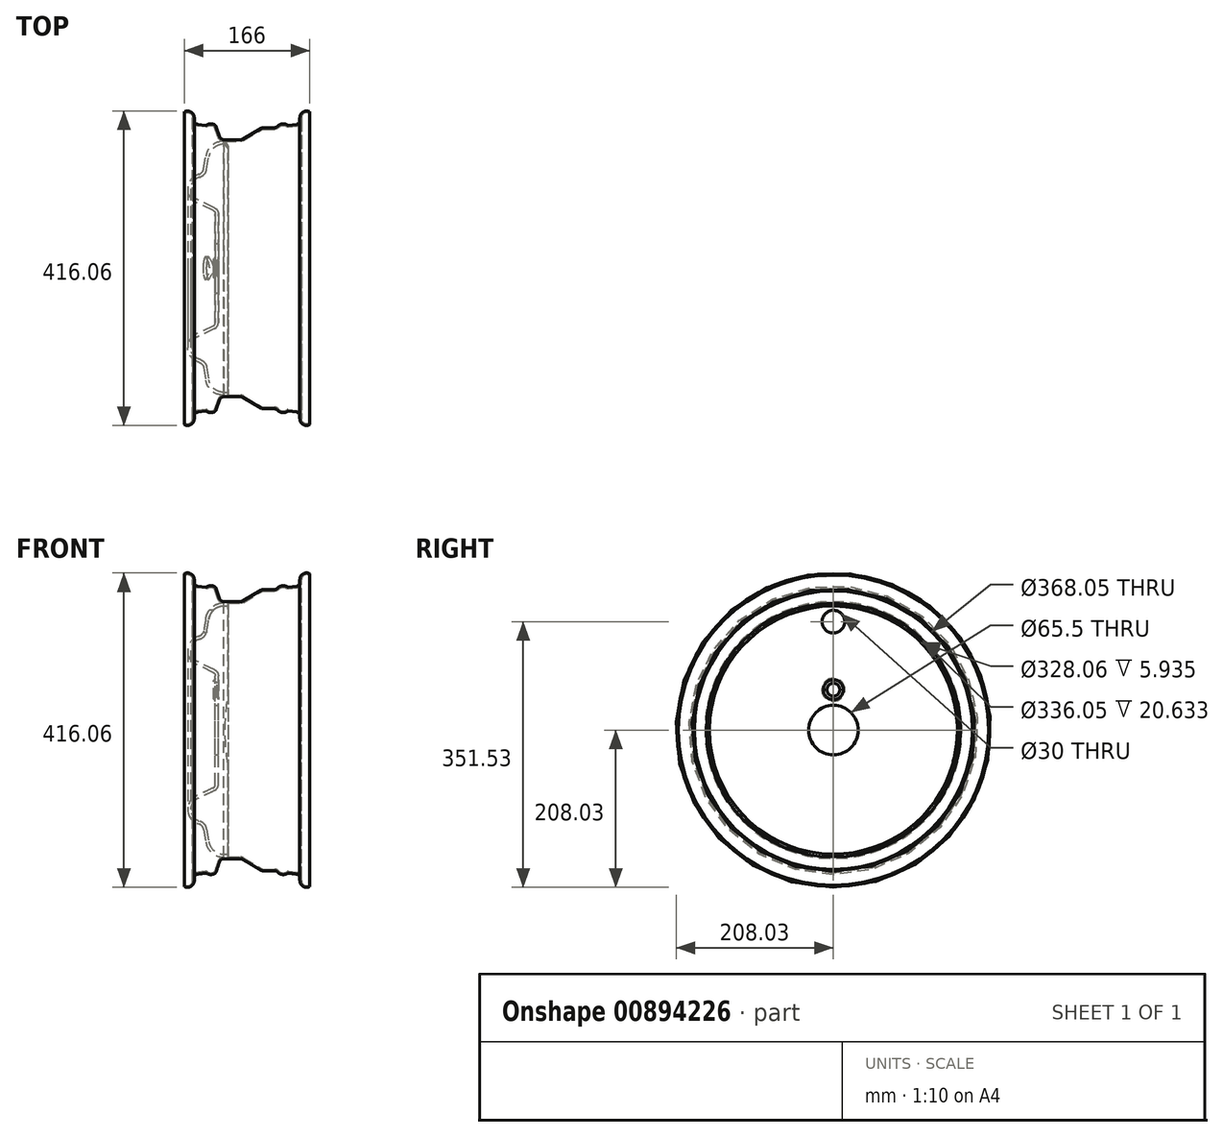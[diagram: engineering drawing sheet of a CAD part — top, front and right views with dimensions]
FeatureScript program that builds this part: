
annotation { "Feature Type Name" : "Feature", "Feature Type Description" : "" }
export const myFeature = defineFeature(function(context is Context, id is Id, definition is map)
    precondition{}
    {
        {
            var Q0;
            Q0=qCreatedBy(makeId("Front.planeOp"),FACE);
            var sketch = newSketch(context, id + "F0", { "sketchPlane" : qUnion([Q0])});
            skLineSegment(sketch, "E0", {"start": v(0, 210) * mm, "end": v(0, 0) * mm});
            skLineSegment(sketch, "E1", {"start": v(85, 0) * mm, "end": v(-85, 0) * mm});
            skArc(sketch, "E2", {"start": v(83, 207) * mm, "mid": v(74.17, 206.72) * mm, "end": v(69.83, 199.03) * mm});
            skArc(sketch, "E3", {"start": v(-69.83, 199.03) * mm, "mid": v(-74.17, 206.72) * mm, "end": v(-83, 207) * mm});
            skLineSegment(sketch, "E4", {"start": v(-8.37, 170.03) * mm, "end": v(-30.69, 170.03) * mm});
            skArc(sketch, "E5", {"start": v(-36.38, 174.1) * mm, "mid": v(-34.2, 171.15) * mm, "end": v(-30.69, 170.03) * mm});
            skLineSegment(sketch, "E6", {"start": v(69.83, 195.43) * mm, "end": v(69.83, 199.03) * mm});
            skArc(sketch, "E7", {"start": v(65.46, 190.47) * mm, "mid": v(68.58, 192.13) * mm, "end": v(69.83, 195.43) * mm});
            skLineSegment(sketch, "E8", {"start": v(54.2, 189.05) * mm, "end": v(65.46, 190.47) * mm});
            skLineSegment(sketch, "E9", {"start": v(36.48, 186.03) * mm, "end": v(21.37, 186.03) * mm});
            skArc(sketch, "E10", {"start": v(21.37, 186.03) * mm, "mid": v(20.05, 185.85) * mm, "end": v(18.82, 185.33) * mm});
            skArc(sketch, "E11", {"start": v(53.84, 189.14) * mm, "mid": v(46.75, 191.05) * mm, "end": v(40.21, 187.7) * mm});
            skArc(sketch, "E12", {"start": v(36.48, 186.03) * mm, "mid": v(38.52, 186.46) * mm, "end": v(40.21, 187.7) * mm});
            skArc(sketch, "E13", {"start": v(53.84, 189.14) * mm, "mid": v(54.01, 189.06) * mm, "end": v(54.2, 189.05) * mm});
            skLineSegment(sketch, "E14", {"start": v(18.82, 185.33) * mm, "end": v(-5.82, 170.72) * mm});
            skArc(sketch, "E15", {"start": v(-8.37, 170.03) * mm, "mid": v(-7.05, 170.2) * mm, "end": v(-5.82, 170.72) * mm});
            skLineSegment(sketch, "E16", {"start": v(-69.83, 195.43) * mm, "end": v(-69.83, 199.03) * mm});
            skLineSegment(sketch, "E17", {"start": v(-54.2, 189.05) * mm, "end": v(-65.46, 190.47) * mm});
            skArc(sketch, "E18", {"start": v(-69.83, 195.43) * mm, "mid": v(-68.58, 192.13) * mm, "end": v(-65.46, 190.47) * mm});
            skArc(sketch, "E19", {"start": v(-43.3, 190.05) * mm, "mid": v(-48.7, 191.07) * mm, "end": v(-53.84, 189.14) * mm});
            skArc(sketch, "E20", {"start": v(-40.77, 187.17) * mm, "mid": v(-41.75, 188.86) * mm, "end": v(-43.3, 190.05) * mm});
            skArc(sketch, "E21", {"start": v(-54.2, 189.05) * mm, "mid": v(-54.01, 189.06) * mm, "end": v(-53.84, 189.14) * mm});
            skLineSegment(sketch, "E22", {"start": v(-36.38, 174.1) * mm, "end": v(-40.77, 187.17) * mm});
            skLineSegment(sketch, "E23", {"start": v(83, 207) * mm, "end": v(82.07, 205.23) * mm});
            skLineSegment(sketch, "E24", {"start": v(-83, 207) * mm, "end": v(-82.07, 205.23) * mm});
            skArc(sketch, "E25", {"start": v(82.07, 205.23) * mm, "mid": v(75.2, 205.01) * mm, "end": v(71.83, 199.03) * mm});
            skLineSegment(sketch, "E26", {"start": v(71.83, 199.03) * mm, "end": v(71.83, 195.43) * mm});
            skArc(sketch, "E27", {"start": v(65.7, 188.49) * mm, "mid": v(70.08, 190.8) * mm, "end": v(71.83, 195.43) * mm});
            skArc(sketch, "E28", {"start": v(52.66, 187.53) * mm, "mid": v(53.51, 187.13) * mm, "end": v(54.45, 187.07) * mm});
            skLineSegment(sketch, "E29", {"start": v(65.7, 188.49) * mm, "end": v(54.45, 187.07) * mm});
            skArc(sketch, "E30", {"start": v(52.66, 187.53) * mm, "mid": v(46.96, 189.07) * mm, "end": v(41.7, 186.37) * mm});
            skArc(sketch, "E31", {"start": v(36.48, 184.03) * mm, "mid": v(39.34, 184.64) * mm, "end": v(41.7, 186.37) * mm});
            skLineSegment(sketch, "E32", {"start": v(36.48, 184.03) * mm, "end": v(21.37, 184.03) * mm});
            skArc(sketch, "E33", {"start": v(21.37, 184.03) * mm, "mid": v(20.58, 183.92) * mm, "end": v(19.84, 183.6) * mm});
            skLineSegment(sketch, "E34", {"start": v(19.84, 183.6) * mm, "end": v(-4.8, 169) * mm});
            skArc(sketch, "E35", {"start": v(-8.37, 168.03) * mm, "mid": v(-6.52, 168.27) * mm, "end": v(-4.8, 169) * mm});
            skLineSegment(sketch, "E36", {"start": v(-8.37, 168.03) * mm, "end": v(-30.69, 168.03) * mm});
            skArc(sketch, "E37", {"start": v(-38.27, 173.47) * mm, "mid": v(-35.36, 169.53) * mm, "end": v(-30.69, 168.03) * mm});
            skLineSegment(sketch, "E38", {"start": v(-38.27, 173.47) * mm, "end": v(-42.67, 186.53) * mm});
            skArc(sketch, "E39", {"start": v(-42.67, 186.53) * mm, "mid": v(-43.25, 187.54) * mm, "end": v(-44.18, 188.26) * mm});
            skArc(sketch, "E40", {"start": v(-44.18, 188.26) * mm, "mid": v(-48.52, 189.08) * mm, "end": v(-52.66, 187.53) * mm});
            skArc(sketch, "E41", {"start": v(-54.45, 187.07) * mm, "mid": v(-53.51, 187.13) * mm, "end": v(-52.66, 187.53) * mm});
            skLineSegment(sketch, "E42", {"start": v(-54.45, 187.07) * mm, "end": v(-65.7, 188.49) * mm});
            skLineSegment(sketch, "E43", {"start": v(-71.83, 195.48) * mm, "end": v(-71.83, 199.03) * mm});
            skArc(sketch, "E44", {"start": v(-71.83, 195.48) * mm, "mid": v(-70.1, 190.82) * mm, "end": v(-65.7, 188.49) * mm});
            skArc(sketch, "E45", {"start": v(-71.83, 199.03) * mm, "mid": v(-75.2, 205.01) * mm, "end": v(-82.07, 205.23) * mm});
            skArc(sketch, "E46", {"start": v(-63.87, 124.27) * mm, "mid": v(-78.43, 106.72) * mm, "end": v(-67.1, 86.94) * mm});
            skArc(sketch, "E47", {"start": v(-63.87, 124.27) * mm, "mid": v(-59.6, 126.91) * mm, "end": v(-57.41, 131.43) * mm});
            skArc(sketch, "E48", {"start": v(-30.51, 168.03) * mm, "mid": v(-46.26, 162.5) * mm, "end": v(-54.6, 148.04) * mm});
            skLineSegment(sketch, "E49", {"start": v(-57.41, 131.43) * mm, "end": v(-54.6, 148.04) * mm});
            skLineSegment(sketch, "E50", {"start": v(-44.85, 76.36) * mm, "end": v(-67.1, 86.94) * mm});
            skLineSegment(sketch, "E51", {"start": v(-42, 71.84) * mm, "end": v(-42, 32.75) * mm});
            skArc(sketch, "E52", {"start": v(-42, 71.84) * mm, "mid": v(-42.77, 74.51) * mm, "end": v(-44.85, 76.36) * mm});
            skLineSegment(sketch, "E53", {"start": v(-25, 168.03) * mm, "end": v(-25, 164.03) * mm});
            skArc(sketch, "E54", {"start": v(-62.8, 120.41) * mm, "mid": v(-74.44, 106.38) * mm, "end": v(-65.37, 90.55) * mm});
            skArc(sketch, "E55", {"start": v(-62.8, 120.41) * mm, "mid": v(-56.63, 124.23) * mm, "end": v(-53.47, 130.76) * mm});
            skArc(sketch, "E56", {"start": v(-30.93, 164.03) * mm, "mid": v(-43.84, 159.3) * mm, "end": v(-50.65, 147.37) * mm});
            skLineSegment(sketch, "E57", {"start": v(-25, 164.03) * mm, "end": v(-30.93, 164.03) * mm});
            skLineSegment(sketch, "E58", {"start": v(-43.13, 79.97) * mm, "end": v(-65.37, 90.55) * mm});
            skLineSegment(sketch, "E59", {"start": v(-53.47, 130.76) * mm, "end": v(-50.65, 147.37) * mm});
            skLineSegment(sketch, "E60", {"start": v(-38, 32.75) * mm, "end": v(-38, 71.84) * mm});
            skArc(sketch, "E61", {"start": v(-38, 71.84) * mm, "mid": v(-39.4, 76.65) * mm, "end": v(-43.13, 79.97) * mm});
            skLineSegment(sketch, "E62", {"start": v(-42, 32.75) * mm, "end": v(-38, 32.75) * mm});
            skSolve(sketch);
        }
        {
            var Q0;
            Q0=qSketchRegion(id+"F0",true);
            var Q1;
            Q1=sQuery(id+"F0.wireOp",EDGE,"E1");
            revolve(context, id + "F1", {"surfaceOperationType" : NewSurfaceOperationType.NEW, "entities" : qUnion([Q0]), "axis" : qUnion([Q1]), "revolveType" : RevolveType.FULL});
        }
        {
            var Q0;
            Q0=qCreatedBy(makeId("Right.planeOp"),FACE);
            var sketch = newSketch(context, id + "F2", { "sketchPlane" : qUnion([Q0])});
            skLineSegment(sketch, "E63", {"start": v(0, 0) * mm, "end": v(0, 143.5) * mm, "construction": true});
            skSolve(sketch);
        }
        {
            var Q0;
            Q0=sQuery(id+"F2.wireOp",VERTEX,"E63.end");
            var Q1;
            Q1=makeQuery(id+"F1.opRevolve","SWEPT_BODY",BODY,{"disambiguationData":[OSD([sQuery(id+"F0.wireOp",EDGE,"E2"),sQuery(id+"F0.wireOp",EDGE,"E3"),sQuery(id+"F0.wireOp",EDGE,"E4"),sQuery(id+"F0.wireOp",EDGE,"E5"),sQuery(id+"F0.wireOp",EDGE,"E6"),sQuery(id+"F0.wireOp",EDGE,"E7"),sQuery(id+"F0.wireOp",EDGE,"E8"),sQuery(id+"F0.wireOp",EDGE,"E9"),sQuery(id+"F0.wireOp",EDGE,"E10"),sQuery(id+"F0.wireOp",EDGE,"E11"),sQuery(id+"F0.wireOp",EDGE,"E12"),sQuery(id+"F0.wireOp",EDGE,"E13"),sQuery(id+"F0.wireOp",EDGE,"E14"),sQuery(id+"F0.wireOp",EDGE,"E15"),sQuery(id+"F0.wireOp",EDGE,"E16"),sQuery(id+"F0.wireOp",EDGE,"E17"),sQuery(id+"F0.wireOp",EDGE,"E18"),sQuery(id+"F0.wireOp",EDGE,"E19"),sQuery(id+"F0.wireOp",EDGE,"E20"),sQuery(id+"F0.wireOp",EDGE,"E21"),sQuery(id+"F0.wireOp",EDGE,"E22"),sQuery(id+"F0.wireOp",EDGE,"E23"),sQuery(id+"F0.wireOp",EDGE,"E24"),sQuery(id+"F0.wireOp",EDGE,"E25"),sQuery(id+"F0.wireOp",EDGE,"E26"),sQuery(id+"F0.wireOp",EDGE,"E27"),sQuery(id+"F0.wireOp",EDGE,"E28"),sQuery(id+"F0.wireOp",EDGE,"E29"),sQuery(id+"F0.wireOp",EDGE,"E30"),sQuery(id+"F0.wireOp",EDGE,"E31"),sQuery(id+"F0.wireOp",EDGE,"E32"),sQuery(id+"F0.wireOp",EDGE,"E33"),sQuery(id+"F0.wireOp",EDGE,"E34"),sQuery(id+"F0.wireOp",EDGE,"E35"),sQuery(id+"F0.wireOp",EDGE,"E36"),sQuery(id+"F0.wireOp",EDGE,"E37"),sQuery(id+"F0.wireOp",EDGE,"E38"),sQuery(id+"F0.wireOp",EDGE,"E39"),sQuery(id+"F0.wireOp",EDGE,"E40"),sQuery(id+"F0.wireOp",EDGE,"E41"),sQuery(id+"F0.wireOp",EDGE,"E42"),sQuery(id+"F0.wireOp",EDGE,"E43"),sQuery(id+"F0.wireOp",EDGE,"E44"),sQuery(id+"F0.wireOp",EDGE,"E45"),sQuery(id+"F0.wireOp",EDGE,"E46"),sQuery(id+"F0.wireOp",EDGE,"E47"),sQuery(id+"F0.wireOp",EDGE,"E48"),sQuery(id+"F0.wireOp",EDGE,"E49"),sQuery(id+"F0.wireOp",EDGE,"E50"),sQuery(id+"F0.wireOp",EDGE,"E51"),sQuery(id+"F0.wireOp",EDGE,"E52"),sQuery(id+"F0.wireOp",EDGE,"E53"),sQuery(id+"F0.wireOp",EDGE,"E54"),sQuery(id+"F0.wireOp",EDGE,"E55"),sQuery(id+"F0.wireOp",EDGE,"E56"),sQuery(id+"F0.wireOp",EDGE,"E57"),sQuery(id+"F0.wireOp",EDGE,"E58"),sQuery(id+"F0.wireOp",EDGE,"E59"),sQuery(id+"F0.wireOp",EDGE,"E60"),sQuery(id+"F0.wireOp",EDGE,"E61"),sQuery(id+"F0.wireOp",EDGE,"E62")])]});
            hole(context, id + "F3", {"style" : HoleStyle.SIMPLE, "endStyle" : HoleEndStyle.THROUGH, "holeDiameter" : 30 * mm, "majorDiameter" : 5 * mm, "isTappedThrough" : true, "tappedDepth" : 12 * mm, "tapClearance" : 3, "locations" : qUnion([Q0]), "scope" : qUnion([Q1]), "startStyle" : HoleStartStyle.PART});
        }
        {
            var Q0;
            Q0=qCreatedBy(makeId("Front.planeOp"),FACE);
            var sketch = newSketch(context, id + "F4", { "sketchPlane" : qUnion([Q0])});
            skArc(sketch, "E64", {"start": v(-44, 66) * mm, "mid": v(-42.52, 67.14) * mm, "end": v(-42, 68.93) * mm});
            skLineSegment(sketch, "E65", {"start": v(-44, 66) * mm, "end": v(-44, 53.5) * mm});
            skLineSegment(sketch, "E66", {"start": v(-44, 53.5) * mm, "end": v(-38.12, 53.5) * mm});
            skLineSegment(sketch, "E67", {"start": v(-42, 68.93) * mm, "end": v(-38.12, 53.5) * mm});
            skSolve(sketch);
        }
        {
            var Q0;
            Q0=makeQuery(id+"F4.imprint","IMPRINT",FACE,{"disambiguationData":[TD([[makeQuery(id+"F4.imprint","IMPRINT",EDGE,{"derivedFrom":sQuery(id+"F4.wireOp",EDGE,"E64")}),-1.0]])]});
            var Q1;
            Q1=sQuery(id+"F4.wireOp",EDGE,"DPuuomy0-pdVH-cpdG-Vd7o-nU3avSwvAgfx");
            var Q2;
            Q2=sQuery(id+"F4.wireOp",EDGE,"E66");
            revolve(context, id + "F5", {"operationType" : NewBodyOperationType.ADD, "surfaceOperationType" : NewSurfaceOperationType.NEW, "entities" : qUnion([Q0]), "surfaceEntities" : qUnion([Q1]), "axis" : qUnion([Q2]), "revolveType" : RevolveType.FULL, "oppositeDirection" : true});
        }
        {
            var Q0;
            Q0=qCreatedBy(makeId("Front.planeOp"),FACE);
            var sketch = newSketch(context, id + "F6", { "sketchPlane" : qUnion([Q0])});
            skArc(sketch, "E68", {"start": v(-40, 62) * mm, "mid": v(-38.48, 64.35) * mm, "end": v(-38, 67.1) * mm});
            skLineSegment(sketch, "E69", {"start": v(-40, 53.5) * mm, "end": v(-38, 53.5) * mm});
            skLineSegment(sketch, "E70", {"start": v(-40, 62) * mm, "end": v(-40, 53.5) * mm});
            skLineSegment(sketch, "E71", {"start": v(-38, 67.1) * mm, "end": v(-38, 53.5) * mm});
            skSolve(sketch);
        }
        {
            var Q0;
            Q0=qSketchRegion(id+"F6",true);
            var Q1;
            Q1=sQuery(id+"F6.wireOp",EDGE,"E69");
            revolve(context, id + "F7", {"operationType" : NewBodyOperationType.REMOVE, "surfaceOperationType" : NewSurfaceOperationType.NEW, "entities" : qUnion([Q0]), "axis" : qUnion([Q1]), "revolveType" : RevolveType.FULL, "oppositeDirection" : true});
        }
        {
            var Q1;
            Q1=makeQuery(id+"F5.opRevolve","SWEPT_FACE",FACE,{"disambiguationData":[OSD([sQuery(id+"F4.wireOp",EDGE,"E65")])]});
            var Q2;
            Q2=makeQuery(id+"F7.boolean.opBoolean","COPY",FACE,{"derivedFrom":makeQuery(id+"F7.opRevolve","SWEPT_FACE",FACE,{"disambiguationData":[OSD([sQuery(id+"F6.wireOp",EDGE,"E70")])]})});
            loft(context, id + "F8", {"operationType" : NewBodyOperationType.REMOVE, "sheetProfilesArray" : [{ "sheetProfileEntities" : qUnion([Q1]) }, { "sheetProfileEntities" : qUnion([Q2]) }]});
        }
        {
            var Q0;
            Q0=qCreatedBy(makeId("Front.planeOp"),FACE);
            var sketch = newSketch(context, id + "F9", { "sketchPlane" : qUnion([Q0])});
            skLineSegment(sketch, "E72", {"start": v(-25, 45) * mm, "end": v(-25, -45) * mm});
            skArc(sketch, "E73", {"start": v(-25, 45) * mm, "mid": v(-29, 0) * mm, "end": v(-25, -45) * mm});
            skLineSegment(sketch, "E74", {"start": v(-25, 0) * mm, "end": v(226.1, 0) * mm, "construction": true});
            skSolve(sketch);
        }
        {
            var Q0;
            Q0=makeQuery(id+"F9.imprint","IMPRINT",FACE,{"disambiguationData":[TD([[makeQuery(id+"F9.imprint","IMPRINT",EDGE,{"derivedFrom":sQuery(id+"F9.wireOp",EDGE,"E72")}),-1.0]])]});
            var Q1;
            Q1=makeQuery(id+"F1.opRevolve","SWEPT_FACE",FACE,{"disambiguationData":[OSD([sQuery(id+"F0.wireOp",EDGE,"E36")])]});
            extrude(context, id + "F10", {"entities" : qUnion([Q0]), "operationType" : NewBodyOperationType.REMOVE, "endBound" : BoundingType.UP_TO_SURFACE, "oppositeDirection" : true, "depth" : 25 * mm, "endBoundEntityFace" : qUnion([Q1]), "offsetDistance" : 25 * mm});
        }
    });
